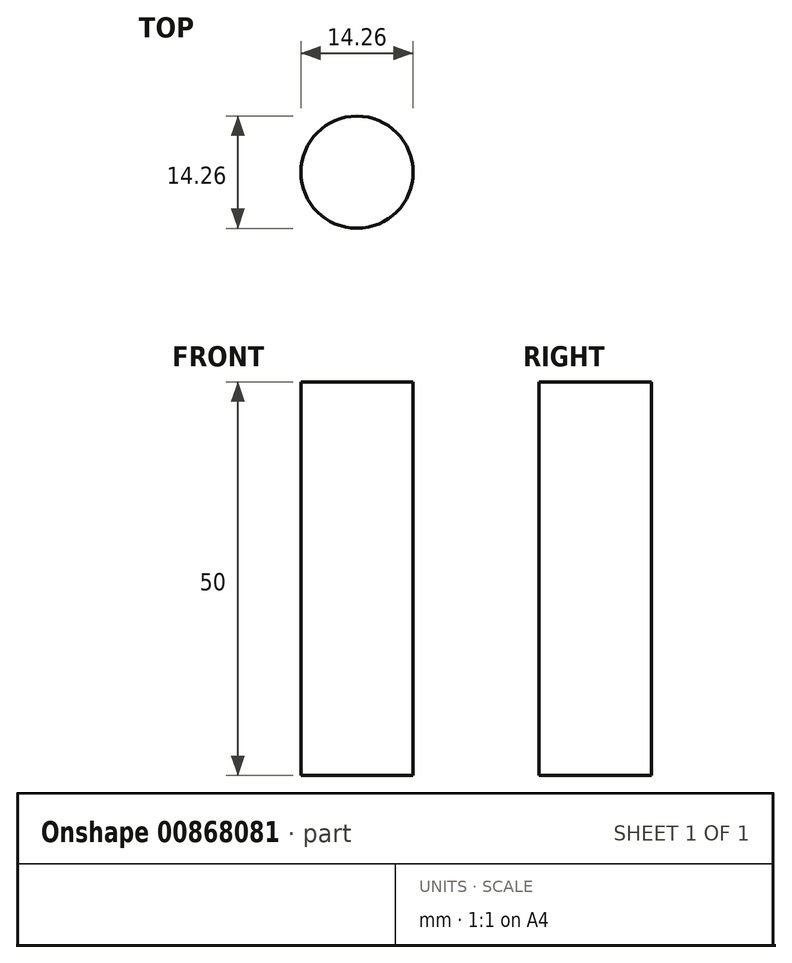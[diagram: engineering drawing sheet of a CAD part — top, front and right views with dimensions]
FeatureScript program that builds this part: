
annotation { "Feature Type Name" : "Feature", "Feature Type Description" : "" }
export const myFeature = defineFeature(function(context is Context, id is Id, definition is map)
    precondition{}
    {
        {
            var Q0;
            Q0=qCreatedBy(makeId("Top.planeOp"),FACE);
            var sketch = newSketch(context, id + "F0", { "sketchPlane" : qUnion([Q0])});
            skCircle(sketch, "E0", {"center": v(0, 0) * mm, "radius": 7.12 * mm});
            skSolve(sketch);
        }
        {
            var Q0;
            Q0 = qSketchRegion(id + "F0", true);
            extrude(context, id + "F1", {"entities" : qUnion([Q0]), "depth" : 50 * mm, "offsetDistance" : 25 * mm});
        }
    });
